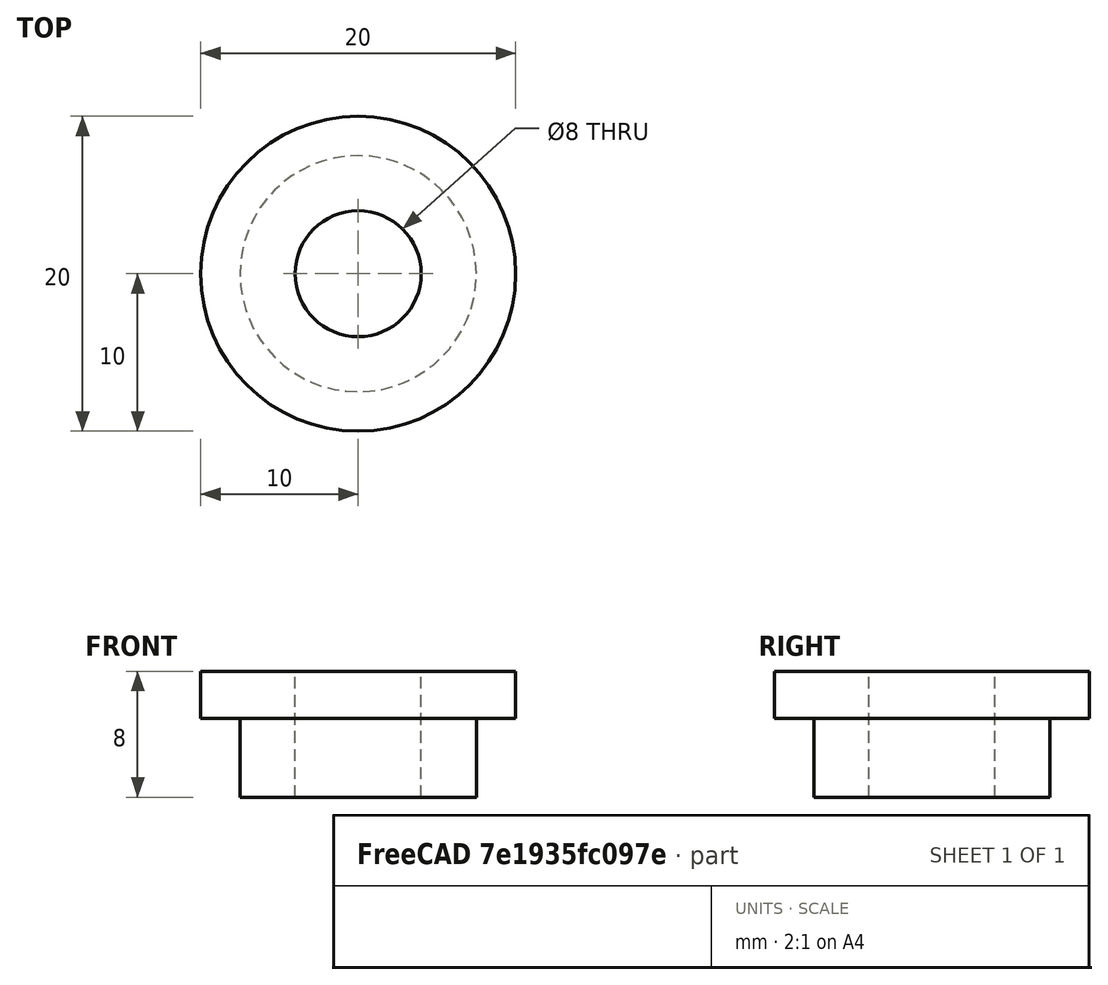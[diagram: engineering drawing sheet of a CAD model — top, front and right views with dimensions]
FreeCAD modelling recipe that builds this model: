
FCSTD DOCUMENT  (FreeCAD 0.19R24267 +148 (Git))
Label: ELEC_P-Pot
License: All rights reserved
LicenseURL: http://en.wikipedia.org/wiki/All_rights_reserved
objects: Sketcher::SketchObject×1, PartDesign::Revolution×1, PartDesign::Body×1
note: 4 computed .brp shape members not serialized (recipe doc carries the construction recipe); baked Part::Feature solids carry a one-line shape summary decoded from their .brp

FEATURE [Sketcher::SketchObject] Sketch
  FullyConstrained = true
  MapMode = 5
  Placement = pos=(0,0,0) rot=(1,0,0;1.5708rad)
  Support = -> [XZ_Plane]
  sketch-geometry (6):
    g0: LineSegment StartX=4 StartY=0 StartZ=0 EndX=4 EndY=8 EndZ=0
    g1: LineSegment StartX=4 StartY=8 StartZ=0 EndX=10 EndY=8 EndZ=0
    g2: LineSegment StartX=10 StartY=8 StartZ=0 EndX=10 EndY=5 EndZ=0
    g3: LineSegment StartX=10 StartY=5 StartZ=0 EndX=7.5 EndY=5 EndZ=0
    g4: LineSegment StartX=7.5 StartY=5 StartZ=0 EndX=7.5 EndY=0 EndZ=0
    g5: LineSegment StartX=7.5 StartY=0 StartZ=0 EndX=4 EndY=0 EndZ=0
  constraints (18):
    c: PointOnObject(g0,g-1)
    c: Vertical(g0)
    c: Coincident(g0,g1)
    c: Horizontal(g1)
    c: Coincident(g1,g2)
    c: Coincident(g2,g3)
    c: Horizontal(g3)
    c: Coincident(g3,g4)
    c: PointOnObject(g4,g-1)
    c: Vertical(g4)
    c: Coincident(g4,g5)
    c: Coincident(g5,g0)
    c: Vertical(g2)
    c: DistanceX(g-1,g0) = 4
    c: DistanceX(g-1,g4) = 7.5
    c: DistanceX(g-1,g2) = 10
    c: DistanceY(g4,g2) = 5
    c: DistanceY(g4,g1) = 8
FEATURE [PartDesign::Revolution] Revolution
  Angle = 360
  Axis = (0,2e-16,1)
  Base = (0,0,0)
  Placement = pos=(0,0,0) rot=(1,0,0;1.5708rad)
  Profile = -> Sketch
  ReferenceAxis = -> Sketch [V_Axis]
  Refine = true
  Reversed = true
FEATURE [PartDesign::Body] Body
  Group = -> [Sketch,Revolution]
  Origin = -> Origin
  Tip = -> Revolution
